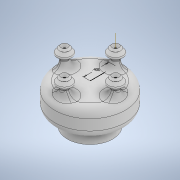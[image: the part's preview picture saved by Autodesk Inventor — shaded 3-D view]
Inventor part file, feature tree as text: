
AUTODESK INVENTOR PART (.ipt)
format: ipt  version: 2020 (Build 240168000, 168)  size: 553,472 bytes
history: native  units: in
note: dims shown in document units (in); Inventor stores cm internally (conversion verified against a paired STEP export)
features: sketch x4, revolve x3, fillet x2, other x1, pattern_circular x1, projected_geometry x1
ambient origin geometry x8: Origin, YZ Plane, XZ Plane, XY Plane, X Axis, Y Axis, Z Axis, Center Point
bodies: Solid1 (feature_tree)
feature tree (12):
  revolve  "Revolution1"  [1 undecoded]
  sketch  "Sketch2"  dims[d2=0.2165in d3=0.0787in]
  other  "Work Axis1"
  revolve  "Revolution2"  [1 undecoded]
  sketch  "Sketch4"  dims[d6=0.1181in d7=0.1181in d9=90.0deg d10=0.4in d11=0.0197in d12=0.1181in d13=0.0in d14=0.0787in d15=135.0deg d16=0.0787in d17=0.0492in d18=0.0394in d20=90.0deg d26=90.0deg d27=1.5748in d28=360.0deg d30=0.0787in d31=0.125in d32=0.0197in d33=90.0deg]
  revolve  "Revolution3"  [1 undecoded]
  pattern_circular  "Circular Pattern1"  [2 undecoded]
  fillet  "Fillet1"  [1 undecoded]
  fillet  "Fillet2"  Radius=0.4in
  sketch  "Sketch1"  dims[d0=0.1575in d1=0.2362in]
  sketch  "Sketch3"  dims[d4=0.1969in d5=0.1969in]
  projected_geometry  "Projected Loop1"
note: 6 required parameter values undecoded (feature->parameter linkage not recoverable at this tier; creation-order binding heuristic only, values carry confidence <= 0.55)